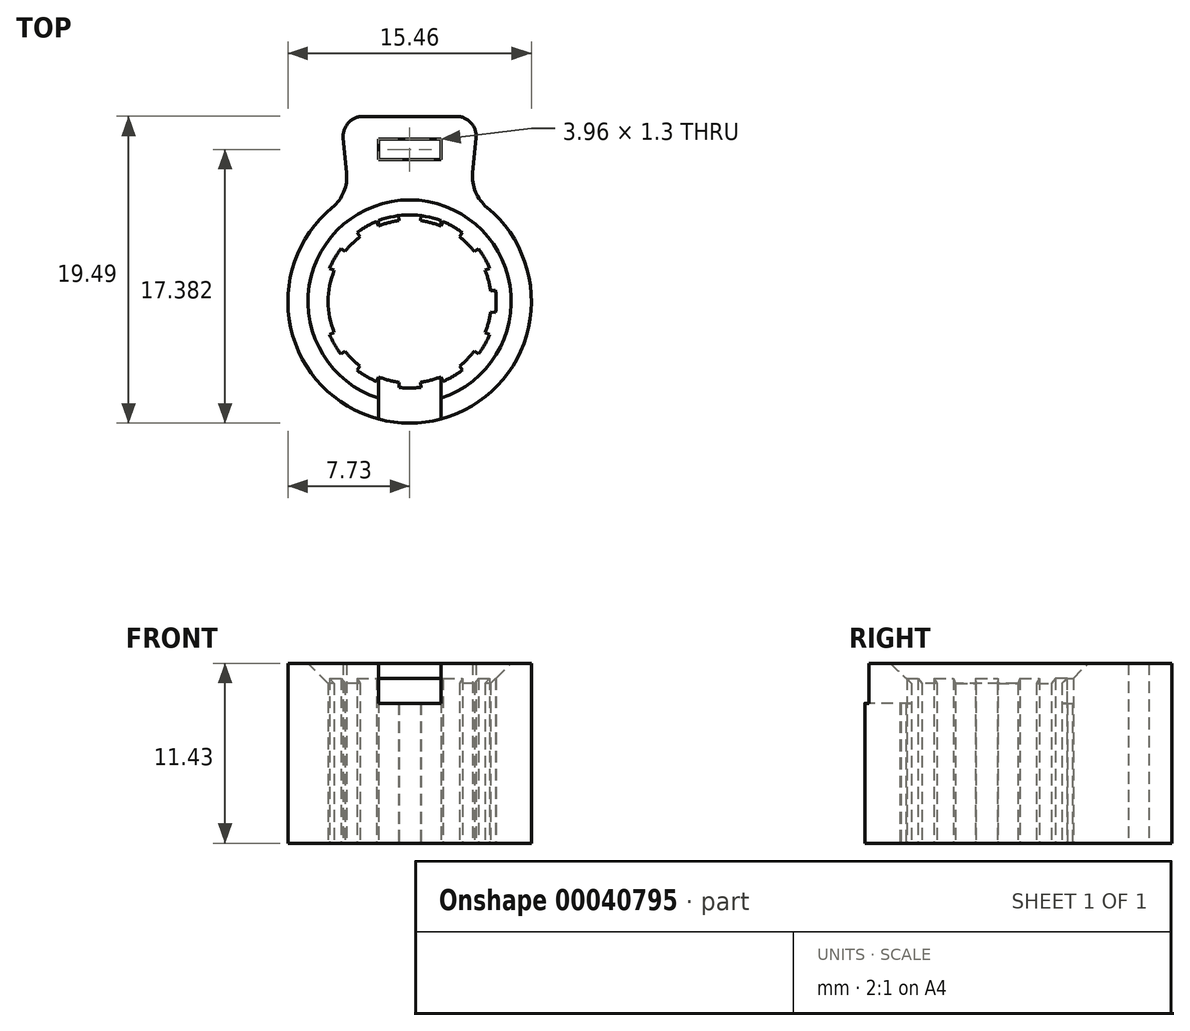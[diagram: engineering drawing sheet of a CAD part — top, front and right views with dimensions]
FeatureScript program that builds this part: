
annotation { "Feature Type Name" : "Feature", "Feature Type Description" : "" }
export const myFeature = defineFeature(function(context is Context, id is Id, definition is map)
    precondition{}
    {
        {
            var Q0;
            Q0=qCreatedBy(makeId("Top.planeOp"),FACE);
            var sketch = newSketch(context, id + "F0", { "sketchPlane" : qUnion([Q0])});
            skCircle(sketch, "E0", {"center": v(0, 0) * mm, "radius": 7.73 * mm});
            skArc(sketch, "E1", {"start": v(-4.79, 1.98) * mm, "mid": v(-5.18, 0) * mm, "end": v(-4.79, -1.98) * mm});
            skCircle(sketch, "E2", {"center": v(0, 0) * mm, "radius": 5.5 * mm});
            skPoint(sketch, "E3", {"position": v(-4.11, 3.15) * mm});
            skPoint(sketch, "E4", {"position": v(-3.15, 4.11) * mm});
            skPoint(sketch, "E5", {"position": v(-1.98, 4.79) * mm});
            skPoint(sketch, "E6", {"position": v(-0.68, 5.14) * mm});
            skPoint(sketch, "E7", {"position": v(0.68, 5.14) * mm});
            skPoint(sketch, "E8", {"position": v(1.98, 4.79) * mm});
            skPoint(sketch, "E9", {"position": v(3.15, 4.11) * mm});
            skPoint(sketch, "E10", {"position": v(4.11, 3.15) * mm});
            skPoint(sketch, "E11", {"position": v(4.79, 1.98) * mm});
            skPoint(sketch, "E12", {"position": v(5.14, 0.68) * mm});
            skPoint(sketch, "E13", {"position": v(5.14, -0.68) * mm});
            skPoint(sketch, "E14", {"position": v(4.79, -1.98) * mm});
            skPoint(sketch, "E15", {"position": v(4.11, -3.15) * mm});
            skPoint(sketch, "E16", {"position": v(3.15, -4.11) * mm});
            skPoint(sketch, "E17", {"position": v(1.98, -4.79) * mm});
            skPoint(sketch, "E18", {"position": v(0.68, -5.14) * mm});
            skPoint(sketch, "E19", {"position": v(-0.68, -5.14) * mm});
            skPoint(sketch, "E20", {"position": v(-1.98, -4.79) * mm});
            skPoint(sketch, "E21", {"position": v(-3.15, -4.11) * mm});
            skPoint(sketch, "E22", {"position": v(-4.11, -3.15) * mm});
            skPoint(sketch, "E23", {"position": v(-4.79, -1.98) * mm});
            skPoint(sketch, "E24", {"position": v(-4.79, 1.98) * mm});
            skArc(sketch, "E25.trimOffspring", {"start": v(-3.15, 4.11) * mm, "mid": v(-3.66, 3.66) * mm, "end": v(-4.11, 3.15) * mm});
            skArc(sketch, "E26.trimOffspring", {"start": v(-0.68, 5.14) * mm, "mid": v(-1.34, 5) * mm, "end": v(-1.98, 4.79) * mm});
            skArc(sketch, "E27.trimOffspring", {"start": v(1.98, 4.79) * mm, "mid": v(1.34, 5) * mm, "end": v(0.68, 5.14) * mm});
            skArc(sketch, "E28.trimOffspring", {"start": v(4.11, 3.15) * mm, "mid": v(3.66, 3.66) * mm, "end": v(3.15, 4.11) * mm});
            skArc(sketch, "E29.trimOffspring", {"start": v(5.14, 0.68) * mm, "mid": v(5, 1.34) * mm, "end": v(4.79, 1.98) * mm});
            skArc(sketch, "E30.trimOffspring", {"start": v(4.79, -1.98) * mm, "mid": v(5, -1.34) * mm, "end": v(5.14, -0.68) * mm});
            skArc(sketch, "E31.trimOffspring", {"start": v(3.15, -4.11) * mm, "mid": v(3.66, -3.66) * mm, "end": v(4.11, -3.15) * mm});
            skArc(sketch, "E32.trimOffspring", {"start": v(0.68, -5.14) * mm, "mid": v(1.34, -5) * mm, "end": v(1.98, -4.79) * mm});
            skArc(sketch, "E33.trimOffspring", {"start": v(-1.98, -4.79) * mm, "mid": v(-1.34, -5) * mm, "end": v(-0.68, -5.14) * mm});
            skArc(sketch, "E34.trimOffspring", {"start": v(-4.11, -3.15) * mm, "mid": v(-3.66, -3.66) * mm, "end": v(-3.15, -4.11) * mm});
            skLineSegment(sketch, "E35", {"start": v(0, 0) * mm, "end": v(-4.79, 1.98) * mm});
            skLineSegment(sketch, "E36", {"start": v(-4.11, 3.15) * mm, "end": v(0, 0) * mm});
            skLineSegment(sketch, "E37", {"start": v(-3.15, 4.11) * mm, "end": v(0, 0) * mm});
            skLineSegment(sketch, "E38", {"start": v(0, 0) * mm, "end": v(-4.79, -1.98) * mm});
            skLineSegment(sketch, "E39", {"start": v(0, 0) * mm, "end": v(-4.11, -3.15) * mm});
            skLineSegment(sketch, "E40", {"start": v(0, 0) * mm, "end": v(-3.15, -4.11) * mm});
            skLineSegment(sketch, "E41", {"start": v(0, 0) * mm, "end": v(-1.98, -4.79) * mm});
            skLineSegment(sketch, "E42", {"start": v(0, 0) * mm, "end": v(-0.68, -5.14) * mm});
            skLineSegment(sketch, "E43", {"start": v(0, 0) * mm, "end": v(0.68, -5.14) * mm});
            skLineSegment(sketch, "E44", {"start": v(0, 0) * mm, "end": v(1.98, -4.79) * mm});
            skLineSegment(sketch, "E45", {"start": v(0, 0) * mm, "end": v(3.15, -4.11) * mm});
            skLineSegment(sketch, "E46", {"start": v(0, 0) * mm, "end": v(4.11, -3.15) * mm});
            skLineSegment(sketch, "E47", {"start": v(0, 0) * mm, "end": v(5.14, 0.68) * mm});
            skLineSegment(sketch, "E48", {"start": v(0, 0) * mm, "end": v(4.79, 1.98) * mm});
            skLineSegment(sketch, "E49", {"start": v(0, 0) * mm, "end": v(4.79, -1.98) * mm});
            skLineSegment(sketch, "E50", {"start": v(0, 0) * mm, "end": v(5.14, -0.68) * mm});
            skLineSegment(sketch, "E51", {"start": v(-1.98, 4.79) * mm, "end": v(0, 0) * mm});
            skLineSegment(sketch, "E52", {"start": v(-0.68, 5.14) * mm, "end": v(0, 0) * mm});
            skLineSegment(sketch, "E53", {"start": v(0.68, 5.14) * mm, "end": v(0, 0) * mm});
            skLineSegment(sketch, "E54", {"start": v(1.98, 4.79) * mm, "end": v(0, 0) * mm});
            skLineSegment(sketch, "E55", {"start": v(3.15, 4.11) * mm, "end": v(0, 0) * mm});
            skLineSegment(sketch, "E56", {"start": v(4.11, 3.15) * mm, "end": v(0, 0) * mm});
            skLineSegment(sketch, "E57", {"start": v(-4.11, 3.15) * mm, "end": v(-4.36, 3.35) * mm});
            skLineSegment(sketch, "E58", {"start": v(-3.15, 4.11) * mm, "end": v(-3.35, 4.36) * mm});
            skLineSegment(sketch, "E59", {"start": v(-4.79, 1.98) * mm, "end": v(-5.08, 2.1) * mm});
            skLineSegment(sketch, "E60", {"start": v(-4.79, -1.98) * mm, "end": v(-5.08, -2.1) * mm});
            skLineSegment(sketch, "E61", {"start": v(-4.11, -3.15) * mm, "end": v(-4.36, -3.35) * mm});
            skLineSegment(sketch, "E62", {"start": v(-3.15, -4.11) * mm, "end": v(-3.35, -4.36) * mm});
            skLineSegment(sketch, "E63", {"start": v(-0.68, -5.14) * mm, "end": v(-0.68, -5.46) * mm});
            skLineSegment(sketch, "E64", {"start": v(0.68, -5.14) * mm, "end": v(0.72, -5.45) * mm});
            skLineSegment(sketch, "E65", {"start": v(1.98, -4.79) * mm, "end": v(2.1, -5.08) * mm});
            skLineSegment(sketch, "E66", {"start": v(3.15, -4.11) * mm, "end": v(3.35, -4.36) * mm});
            skLineSegment(sketch, "E67", {"start": v(4.11, -3.15) * mm, "end": v(4.36, -3.35) * mm});
            skLineSegment(sketch, "E68", {"start": v(4.79, -1.98) * mm, "end": v(5.08, -2.1) * mm});
            skLineSegment(sketch, "E69", {"start": v(5.14, -0.68) * mm, "end": v(5.45, -0.72) * mm});
            skLineSegment(sketch, "E70", {"start": v(5.14, 0.68) * mm, "end": v(5.45, 0.72) * mm});
            skLineSegment(sketch, "E71", {"start": v(4.79, 1.98) * mm, "end": v(5.08, 2.1) * mm});
            skLineSegment(sketch, "E72", {"start": v(4.11, 3.15) * mm, "end": v(4.36, 3.35) * mm});
            skLineSegment(sketch, "E73", {"start": v(3.15, 4.11) * mm, "end": v(3.35, 4.36) * mm});
            skLineSegment(sketch, "E74", {"start": v(1.98, 4.79) * mm, "end": v(2.1, 5.08) * mm});
            skLineSegment(sketch, "E75", {"start": v(0.68, 5.14) * mm, "end": v(0.72, 5.45) * mm});
            skLineSegment(sketch, "E76", {"start": v(-0.68, 5.14) * mm, "end": v(-0.72, 5.45) * mm});
            skLineSegment(sketch, "E77", {"start": v(-1.98, 4.79) * mm, "end": v(-2.1, 5.08) * mm});
            skLineSegment(sketch, "E78", {"start": v(-1.98, -4.79) * mm, "end": v(-2.1, -5.08) * mm});
            skLineSegment(sketch, "E79", {"start": v(0, 0) * mm, "end": v(0, 7.73) * mm});
            skLineSegment(sketch, "E80", {"start": v(-3.86, 6.7) * mm, "end": v(-4.36, 11.76) * mm});
            skLineSegment(sketch, "E81", {"start": v(-4.36, 11.76) * mm, "end": v(4.36, 11.76) * mm});
            skLineSegment(sketch, "E82", {"start": v(4.36, 11.76) * mm, "end": v(3.86, 6.7) * mm});
            skLineSegment(sketch, "E83.bottom", {"start": v(1.98, 9) * mm, "end": v(-1.98, 9) * mm});
            skLineSegment(sketch, "E83.top", {"start": v(1.98, 10.3) * mm, "end": v(-1.98, 10.3) * mm});
            skLineSegment(sketch, "E83.left", {"start": v(1.98, 9) * mm, "end": v(1.98, 10.3) * mm});
            skLineSegment(sketch, "E83.right", {"start": v(-1.98, 9) * mm, "end": v(-1.98, 10.3) * mm});
            skPoint(sketch, "E83.middle", {"position": v(0, 9.65) * mm});
            skSolve(sketch);
        }
        {
            var Q0;
            Q0=makeQuery(id+"F0.imprint","IMPRINT",FACE,{"disambiguationData":[TD([[makeQuery(id+"F0.imprint","IMPRINT",EDGE,{"derivedFrom":sQuery(id+"F0.wireOp",EDGE,"ttt8ZF1X-dX10-uhzB-NxvQ-CnsZi1ClNVwv")}),1.0]])]});
            var Q1;
            {var subQ4=sQuery(id+"F0.wireOp",EDGE,"c5Dz658Q-dkep-xTCV-CCGw-quUJI2YEMZ8H.bottom");Q1=makeQuery(id+"F0.imprint","IMPRINT",FACE,{"disambiguationData":[TD([[makeQuery(id+"F0.imprint","IMPRINT",EDGE,{"derivedFrom":subQ4}),-1.0]])]});}
            var Q2;
            Q2=makeQuery(id+"F0.imprint","IMPRINT",FACE,{"disambiguationData":[TD([[makeQuery(id+"F0.imprint","IMPRINT",EDGE,{"derivedFrom":sQuery(id+"F0.wireOp",EDGE,"E0")}),1.0]])]});
            var Q3;
            {var subQ0=sQuery(id+"F0.wireOp",EDGE,"E80");Q3=makeQuery(id+"F0.imprint","IMPRINT",FACE,{"disambiguationData":[TD([[makeQuery(id+"F0.imprint","IMPRINT",EDGE,{"derivedFrom":subQ0}),-1.0]])]});}
            extrude(context, id + "F1", {"entities" : qUnion([Q0, Q1, Q2, Q3]), "depth" : 11.43 * mm});
        }
        {
            var Q0;
            Q0=makeQuery(id+"F1.opExtrude","SWEPT_EDGE",EDGE,{"disambiguationData":[OSD([sQuery(id+"F0.wireOp",EDGE,"E0"),sQuery(id+"F0.wireOp",EDGE,"E82")])]});
            var Q1;
            Q1=makeQuery(id+"F1.opExtrude","SWEPT_EDGE",EDGE,{"disambiguationData":[OSD([sQuery(id+"F0.wireOp",EDGE,"E0"),sQuery(id+"F0.wireOp",EDGE,"E80")])]});
            fillet(context, id + "F2", {"entities" : qUnion([Q0, Q1]), "radius" : 2.54 * mm, "tangentPropagation" : true, "allowEdgeOverflow" : false});
        }
        {
            var Q0;
            Q0=makeQuery(id+"F1.opExtrude","CAP_FACE",FACE,{"disambiguationData":[OSD([sQuery(id+"F0.wireOp",EDGE,"E0"),sQuery(id+"F0.wireOp",EDGE,"E1"),sQuery(id+"F0.wireOp",EDGE,"E2"),sQuery(id+"F0.wireOp",EDGE,"E25.trimOffspring"),sQuery(id+"F0.wireOp",EDGE,"E26.trimOffspring"),sQuery(id+"F0.wireOp",EDGE,"E27.trimOffspring"),sQuery(id+"F0.wireOp",EDGE,"E28.trimOffspring"),sQuery(id+"F0.wireOp",EDGE,"E29.trimOffspring"),sQuery(id+"F0.wireOp",EDGE,"E30.trimOffspring"),sQuery(id+"F0.wireOp",EDGE,"E31.trimOffspring"),sQuery(id+"F0.wireOp",EDGE,"E32.trimOffspring"),sQuery(id+"F0.wireOp",EDGE,"E33.trimOffspring"),sQuery(id+"F0.wireOp",EDGE,"E34.trimOffspring"),sQuery(id+"F0.wireOp",EDGE,"E57"),sQuery(id+"F0.wireOp",EDGE,"E58"),sQuery(id+"F0.wireOp",EDGE,"E59"),sQuery(id+"F0.wireOp",EDGE,"E60"),sQuery(id+"F0.wireOp",EDGE,"E61"),sQuery(id+"F0.wireOp",EDGE,"E62"),sQuery(id+"F0.wireOp",EDGE,"E63"),sQuery(id+"F0.wireOp",EDGE,"E64"),sQuery(id+"F0.wireOp",EDGE,"E65"),sQuery(id+"F0.wireOp",EDGE,"E66"),sQuery(id+"F0.wireOp",EDGE,"E67"),sQuery(id+"F0.wireOp",EDGE,"E68"),sQuery(id+"F0.wireOp",EDGE,"E69"),sQuery(id+"F0.wireOp",EDGE,"E70"),sQuery(id+"F0.wireOp",EDGE,"E71"),sQuery(id+"F0.wireOp",EDGE,"E72"),sQuery(id+"F0.wireOp",EDGE,"E73"),sQuery(id+"F0.wireOp",EDGE,"E74"),sQuery(id+"F0.wireOp",EDGE,"E75"),sQuery(id+"F0.wireOp",EDGE,"E76"),sQuery(id+"F0.wireOp",EDGE,"E77"),sQuery(id+"F0.wireOp",EDGE,"E78"),sQuery(id+"F0.wireOp",EDGE,"E80"),sQuery(id+"F0.wireOp",EDGE,"E81"),sQuery(id+"F0.wireOp",EDGE,"E82"),sQuery(id+"F0.wireOp",EDGE,"E83.bottom"),sQuery(id+"F0.wireOp",EDGE,"E83.top"),sQuery(id+"F0.wireOp",EDGE,"E83.left"),sQuery(id+"F0.wireOp",EDGE,"E83.right")])],"isStart":false});
            var sketch = newSketch(context, id + "F3", { "sketchPlane" : qUnion([Q0])});
            skLineSegment(sketch, "E84.0", {"start": v(1.98, 9) * mm, "end": v(-1.98, 9) * mm});
            skLineSegment(sketch, "E85.bottom", {"start": v(-1.98, 9) * mm, "end": v(1.98, 9) * mm});
            skLineSegment(sketch, "E85.top", {"start": v(-1.98, -8.92) * mm, "end": v(1.98, -8.92) * mm});
            skLineSegment(sketch, "E85.left", {"start": v(-1.98, 9) * mm, "end": v(-1.98, -8.92) * mm});
            skLineSegment(sketch, "E85.right", {"start": v(1.98, 9) * mm, "end": v(1.98, -8.92) * mm});
            skSolve(sketch);
        }
        {
            var Q0;
            Q0=makeQuery(id+"F0.imprint","IMPRINT",FACE,{"disambiguationData":[TD([[makeQuery(id+"F0.imprint","IMPRINT",EDGE,{"derivedFrom":sQuery(id+"F0.wireOp",EDGE,"E25.trimOffspring")}),-1.0]])]});
            var Q1;
            Q1=makeQuery(id+"F0.imprint","IMPRINT",FACE,{"disambiguationData":[TD([[makeQuery(id+"F0.imprint","IMPRINT",EDGE,{"derivedFrom":sQuery(id+"F0.wireOp",EDGE,"E26.trimOffspring")}),-1.0]])]});
            var Q2;
            Q2=makeQuery(id+"F0.imprint","IMPRINT",FACE,{"disambiguationData":[TD([[makeQuery(id+"F0.imprint","IMPRINT",EDGE,{"derivedFrom":sQuery(id+"F0.wireOp",EDGE,"E27.trimOffspring")}),-1.0]])]});
            var Q3;
            Q3=makeQuery(id+"F0.imprint","IMPRINT",FACE,{"disambiguationData":[TD([[makeQuery(id+"F0.imprint","IMPRINT",EDGE,{"derivedFrom":sQuery(id+"F0.wireOp",EDGE,"E28.trimOffspring")}),-1.0]])]});
            var Q4;
            Q4=makeQuery(id+"F0.imprint","IMPRINT",FACE,{"disambiguationData":[TD([[makeQuery(id+"F0.imprint","IMPRINT",EDGE,{"derivedFrom":sQuery(id+"F0.wireOp",EDGE,"E29.trimOffspring")}),-1.0]])]});
            var Q5;
            Q5=makeQuery(id+"F0.imprint","IMPRINT",FACE,{"disambiguationData":[TD([[makeQuery(id+"F0.imprint","IMPRINT",EDGE,{"derivedFrom":sQuery(id+"F0.wireOp",EDGE,"E1")}),-1.0]])]});
            var Q6;
            Q6=makeQuery(id+"F0.imprint","IMPRINT",FACE,{"disambiguationData":[TD([[makeQuery(id+"F0.imprint","IMPRINT",EDGE,{"derivedFrom":sQuery(id+"F0.wireOp",EDGE,"E34.trimOffspring")}),-1.0]])]});
            var Q7;
            Q7=makeQuery(id+"F0.imprint","IMPRINT",FACE,{"disambiguationData":[TD([[makeQuery(id+"F0.imprint","IMPRINT",EDGE,{"derivedFrom":sQuery(id+"F0.wireOp",EDGE,"E33.trimOffspring")}),-1.0]])]});
            var Q8;
            Q8=makeQuery(id+"F0.imprint","IMPRINT",FACE,{"disambiguationData":[TD([[makeQuery(id+"F0.imprint","IMPRINT",EDGE,{"derivedFrom":sQuery(id+"F0.wireOp",EDGE,"E32.trimOffspring")}),-1.0]])]});
            var Q9;
            Q9=makeQuery(id+"F0.imprint","IMPRINT",FACE,{"disambiguationData":[TD([[makeQuery(id+"F0.imprint","IMPRINT",EDGE,{"derivedFrom":sQuery(id+"F0.wireOp",EDGE,"E31.trimOffspring")}),-1.0]])]});
            var Q10;
            Q10=makeQuery(id+"F0.imprint","IMPRINT",FACE,{"disambiguationData":[TD([[makeQuery(id+"F0.imprint","IMPRINT",EDGE,{"derivedFrom":sQuery(id+"F0.wireOp",EDGE,"E30.trimOffspring")}),-1.0]])]});
            extrude(context, id + "F4", {"entities" : qUnion([Q0, Q1, Q2, Q3, Q4, Q5, Q6, Q7, Q8, Q9, Q10]), "operationType" : NewBodyOperationType.ADD, "depth" : 11.43 * mm});
        }
        {
            var Q0;
            {var subQ0=sQuery(id+"F3.wireOp",EDGE,"E85.bottom");Q0=makeQuery(id+"F3.imprint","IMPRINT",FACE,{"disambiguationData":[TD([[makeQuery(id+"F3.imprint","IMPRINT",EDGE,{"derivedFrom":subQ0}),1.0]])]});}
            var Q1;
            {var subQ0=sQuery(id+"F3.wireOp",EDGE,"E85.left");var subQ1=makeQuery(id+"F1.opExtrude","CAP_EDGE",EDGE,{"disambiguationData":[OSD([sQuery(id+"F0.wireOp",EDGE,"E2")])],"isStart":false});var subQ2=makeQuery(id+"F3.imprint","INTERSECT",VERTEX,{"disambiguationData":[OD(0.0)],"derivedFrom":[subQ1,subQ0]});Q1=makeQuery(id+"F3.imprint","IMPRINT",FACE,{"disambiguationData":[TD([[makeQuery(id+"F3.imprint","IMPRINT",EDGE,{"disambiguationData":[TD([[subQ2,-1.0]])],"derivedFrom":subQ0}),1.0]])]});}
            var Q2;
            {var subQ0=sQuery(id+"F3.wireOp",EDGE,"E85.left");var subQ1=makeQuery(id+"F1.opExtrude","CAP_EDGE",EDGE,{"disambiguationData":[OSD([sQuery(id+"F0.wireOp",EDGE,"E0")])],"isStart":false});var subQ2=makeQuery(id+"F3.imprint","INTERSECT",VERTEX,{"derivedFrom":[subQ1,subQ0]});Q2=makeQuery(id+"F3.imprint","IMPRINT",FACE,{"disambiguationData":[TD([[makeQuery(id+"F3.imprint","IMPRINT",EDGE,{"disambiguationData":[TD([[subQ2,1.0]])],"derivedFrom":subQ0}),1.0]])]});}
            extrude(context, id + "F5", {"entities" : qUnion([Q0, Q1, Q2]), "operationType" : NewBodyOperationType.REMOVE, "oppositeDirection" : true, "depth" : 2.54 * mm});
        }
        {
            var Q0;
            Q0=makeQuery(id+"F4.opExtrude","CAP_EDGE",EDGE,{"disambiguationData":[OSD([sQuery(id+"F0.wireOp",EDGE,"E1")])],"isStart":false});
            var Q1;
            Q1=makeQuery(id+"F4.opExtrude","CAP_EDGE",EDGE,{"disambiguationData":[OSD([sQuery(id+"F0.wireOp",EDGE,"E34.trimOffspring")])],"isStart":false});
            var Q2;
            Q2=makeQuery(id+"F4.opExtrude","CAP_EDGE",EDGE,{"disambiguationData":[OSD([sQuery(id+"F0.wireOp",EDGE,"E25.trimOffspring")])],"isStart":false});
            var Q3;
            Q3=makeQuery(id+"F4.opExtrude","CAP_EDGE",EDGE,{"disambiguationData":[OSD([sQuery(id+"F0.wireOp",EDGE,"E28.trimOffspring")])],"isStart":false});
            var Q4;
            Q4=makeQuery(id+"F4.opExtrude","CAP_EDGE",EDGE,{"disambiguationData":[OSD([sQuery(id+"F0.wireOp",EDGE,"E29.trimOffspring")])],"isStart":false});
            var Q5;
            Q5=makeQuery(id+"F4.opExtrude","CAP_EDGE",EDGE,{"disambiguationData":[OSD([sQuery(id+"F0.wireOp",EDGE,"E30.trimOffspring")])],"isStart":false});
            var Q6;
            Q6=makeQuery(id+"F4.opExtrude","CAP_EDGE",EDGE,{"disambiguationData":[OSD([sQuery(id+"F0.wireOp",EDGE,"E31.trimOffspring")])],"isStart":false});
            chamfer(context, id + "F6", {"entities" : qUnion([Q0, Q1, Q2, Q3, Q4, Q5, Q6]), "width" : 1.27 * mm, "tangentPropagation" : true});
        }
        {
            var Q0;
            Q0=makeQuery(id+"F1.opExtrude","SWEPT_EDGE",EDGE,{"disambiguationData":[OSD([sQuery(id+"F0.wireOp",EDGE,"E80"),sQuery(id+"F0.wireOp",EDGE,"E81")])]});
            var Q1;
            Q1=makeQuery(id+"F1.opExtrude","SWEPT_EDGE",EDGE,{"disambiguationData":[OSD([sQuery(id+"F0.wireOp",EDGE,"E81"),sQuery(id+"F0.wireOp",EDGE,"E82")])]});
            fillet(context, id + "F7", {"entities" : qUnion([Q0, Q1]), "radius" : 1.27 * mm, "tangentPropagation" : true, "allowEdgeOverflow" : false});
        }
    });
